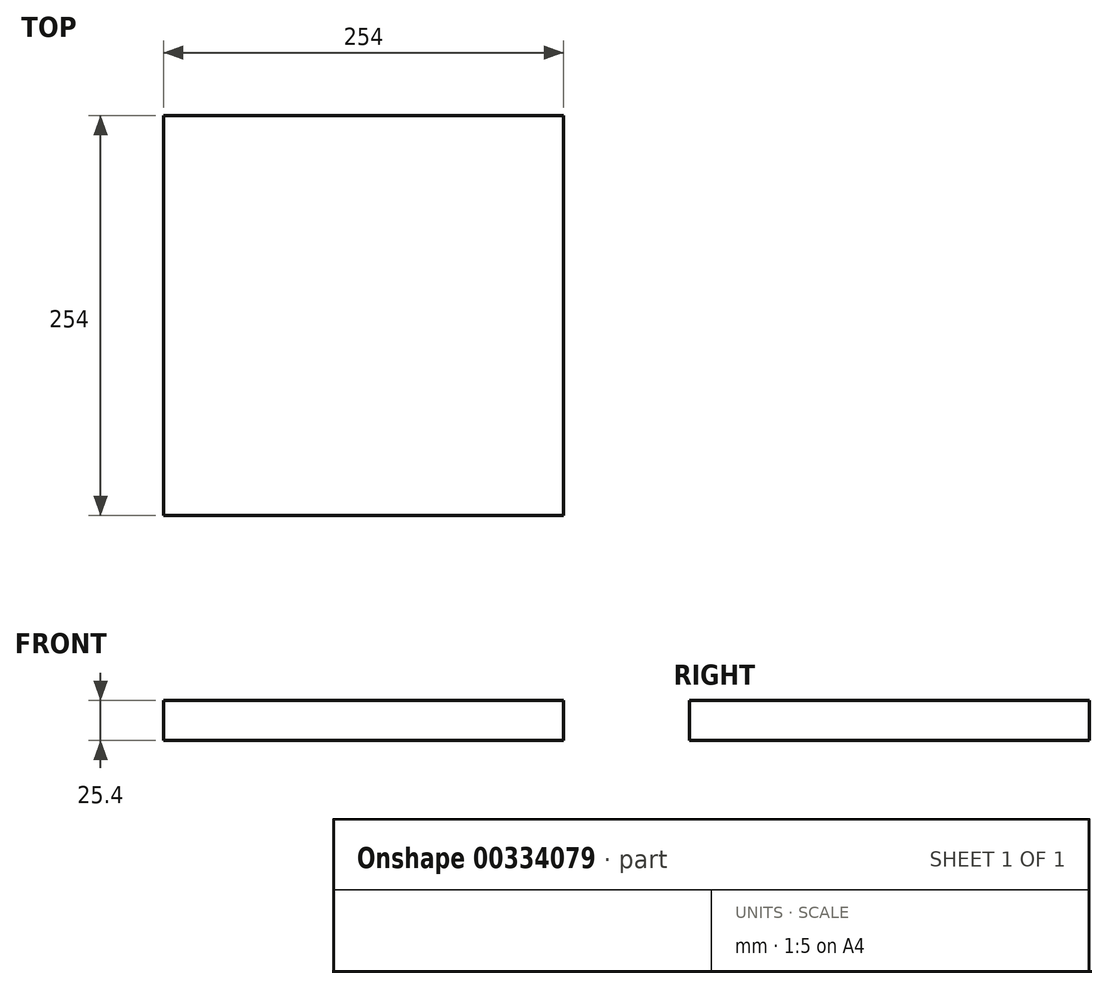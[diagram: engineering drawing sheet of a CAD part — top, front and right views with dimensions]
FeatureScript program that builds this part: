
annotation { "Feature Type Name" : "Feature", "Feature Type Description" : "" }
export const myFeature = defineFeature(function(context is Context, id is Id, definition is map)
    precondition{}
    {
        {
            var Q0;
            Q0=qCreatedBy(makeId("Top.planeOp"),FACE);
            var sketch = newSketch(context, id + "F0", { "sketchPlane" : qUnion([Q0])});
            skLineSegment(sketch, "E0.bottom", {"start": v(0, 0) * mm, "end": v(254, 0) * mm});
            skLineSegment(sketch, "E0.top", {"start": v(0, 254) * mm, "end": v(254, 254) * mm});
            skLineSegment(sketch, "E0.left", {"start": v(0, 0) * mm, "end": v(0, 254) * mm});
            skLineSegment(sketch, "E0.right", {"start": v(254, 0) * mm, "end": v(254, 254) * mm});
            skSolve(sketch);
        }
        {
            var Q0;
            Q0 = qSketchRegion(id + "F0", true);
            extrude(context, id + "F1", {"entities" : qUnion([Q0]), "depth" : 25.4 * mm});
        }
    });
